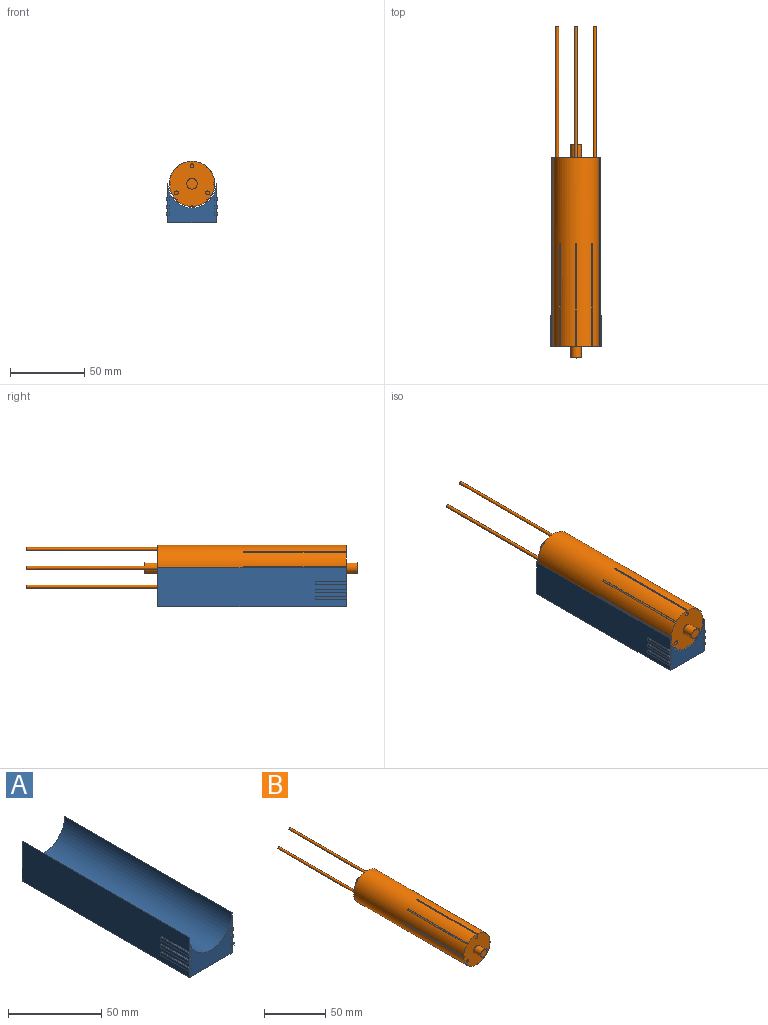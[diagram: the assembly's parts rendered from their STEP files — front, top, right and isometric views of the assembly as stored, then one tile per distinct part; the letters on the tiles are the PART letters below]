
ASSEMBLY  parts=2 mates=1
PART A: 42 faces, bbox 34.5x127.5x26.3 mm
  f0: plane 127x26.3mm, normal (-1,0,0), area 3216.9mm2, adj f1,f2,f3,f5,f6,f7,f8,f12
  f1: plane 32.51x26.3mm, normal (0,-1,0), area 428.4mm2, adj f0,f2,f3,f4,f7,f8,f9,f13
  f2: cylinder r=16.26mm len=127mm, axis (0,1,0), area 6485.9mm2, adj f0,f1,f4,f5
  f3: plane 127x32.51mm, normal (0,0,-1), area 4129mm2, adj f0,f1,f4,f5
  f4: plane 127x26.3mm, normal (1,0,0), area 3216.9mm2, adj f1,f2,f3,f5,f24,f26,f29,f30
  f5: plane 32.51x26.3mm, normal (0,1,0), area 439.8mm2, adj f0,f2,f3,f4
  f6: plane 1.96x0.98mm, normal (0,1,0), area 1.9mm2, adj f0,f7,f8,f10
  f7: plane 21.31x1.96mm, normal (0,0,1), area 21.4mm2, adj f0,f1,f6,f9,f10,f11
  f8: plane 21.31x1.96mm, normal (0,0,-1), area 21.4mm2, adj f0,f1,f6,f9,f10,f11
  f9: plane 1.96x0.48mm, normal (1,0,0), area 0.9mm2, adj f1,f7,f8,f11
  f10: plane 21.31x1.96mm, normal (-1,0,0), area 41.8mm2, adj f6,f7,f8,f11
  f11: plane 1.96x1.96mm, normal (0,-1,0), area 3.9mm2, adj f7,f8,f9,f10
  f12: plane 1.96x0.99mm, normal (0,1,0), area 1.9mm2, adj f0,f13,f14,f16
  f13: plane 21.31x1.96mm, normal (0,0,-1), area 21.6mm2, adj f0,f1,f12,f15,f16,f17
  f14: plane 21.31x1.96mm, normal (0,0,1), area 21.6mm2, adj f0,f1,f12,f15,f16,f17
  f15: plane 1.96x0.48mm, normal (1,0,0), area 0.9mm2, adj f1,f13,f14,f17
  f16: plane 21.31x1.96mm, normal (-1,0,0), area 41.8mm2, adj f12,f13,f14,f17
  f17: plane 1.96x1.96mm, normal (0,-1,0), area 3.9mm2, adj f13,f14,f15,f16
  f18: plane 1.96x1mm, normal (0,1,0), area 2mm2, adj f0,f19,f20,f22
  f19: plane 21.31x1.96mm, normal (0,0,-1), area 21.8mm2, adj f0,f1,f18,f21,f22,f23
  f20: plane 21.31x1.96mm, normal (0,0,1), area 21.8mm2, adj f0,f1,f18,f21,f22,f23
  f21: plane 1.96x0.48mm, normal (1,0,0), area 0.9mm2, adj f1,f19,f20,f23
  f22: plane 21.31x1.96mm, normal (-1,0,0), area 41.8mm2, adj f18,f19,f20,f23
  f23: plane 1.96x1.96mm, normal (0,-1,0), area 3.9mm2, adj f19,f20,f21,f22
  f24: plane 21.31x1.96mm, normal (0,0,1), area 21.6mm2, adj f1,f4,f25,f27,f28,f29
  f25: plane 1.96x0.48mm, normal (-1,0,0), area 0.9mm2, adj f1,f24,f26,f28
  f26: plane 21.31x1.96mm, normal (0,0,-1), area 21.6mm2, adj f1,f4,f25,f27,f28,f29
  f27: plane 21.31x1.96mm, normal (1,0,0), area 41.8mm2, adj f24,f26,f28,f29
  f28: plane 1.96x1.96mm, normal (0,-1,0), area 3.9mm2, adj f24,f25,f26,f27
  f29: plane 1.96x0.99mm, normal (0,1,0), area 1.9mm2, adj f4,f24,f26,f27
  f30: plane 21.31x1.96mm, normal (0,0,1), area 21.8mm2, adj f1,f4,f31,f33,f34,f35
  f31: plane 1.96x0.48mm, normal (-1,0,0), area 0.9mm2, adj f1,f30,f32,f34
  f32: plane 21.31x1.96mm, normal (0,0,-1), area 21.8mm2, adj f1,f4,f31,f33,f34,f35
  f33: plane 21.31x1.96mm, normal (1,0,0), area 41.8mm2, adj f30,f32,f34,f35
  f34: plane 1.96x1.96mm, normal (0,-1,0), area 3.9mm2, adj f30,f31,f32,f33
  f35: plane 1.96x1mm, normal (0,1,0), area 2mm2, adj f4,f30,f32,f33
  f36: plane 21.31x1.96mm, normal (0,0,1), area 21.4mm2, adj f1,f4,f37,f39,f40,f41
  f37: plane 1.96x0.48mm, normal (-1,0,0), area 0.9mm2, adj f1,f36,f38,f40
  f38: plane 21.31x1.96mm, normal (0,0,-1), area 21.4mm2, adj f1,f4,f37,f39,f40,f41
  f39: plane 21.31x1.96mm, normal (1,0,0), area 41.8mm2, adj f36,f38,f40,f41
  f40: plane 1.96x1.96mm, normal (0,-1,0), area 3.9mm2, adj f36,f37,f38,f39
  f41: plane 1.96x0.98mm, normal (0,1,0), area 1.9mm2, adj f4,f36,f38,f39
PART B: 53 faces, bbox 30.5x223.9x30.5 mm
  f0: cylinder r=15.24mm len=127mm, axis (0,1,0), area 11539.3mm2, adj f1,f2,f13,f14,f15,f17,f18,f19
  f1: plane 30.46x30.46mm, normal (0,-1,0), area 670.3mm2, adj f0,f5,f7,f9,f11,f14,f15,f16
  f2: plane 30.48x30.48mm, normal (0,1,0), area 676.7mm2, adj f0,f4,f45,f47,f49,f51
  f3: plane 7.13x7.13mm, normal (0,1,0), area 40mm2, adj f4
  f4: cylinder r=3.57mm len=9.14mm, axis (0,1,0), area 204.9mm2, adj f2,f3
  f5: cylinder r=3.57mm len=7.95mm, axis (0,1,0), area 178.2mm2, adj f1,f6
  f6: plane 7.13x7.13mm, normal (0,-1,0), area 40mm2, adj f5
  f7: cylinder r=1.27mm len=5.08mm, axis (0,-1,0), area 40.5mm2, adj f1,f8
  f8: plane 2.54x2.54mm, normal (0,-1,0), area 5.1mm2, adj f7
  f9: cylinder r=1.27mm len=5.08mm, axis (0,-1,0), area 40.5mm2, adj f1,f10
  f10: plane 2.54x2.54mm, normal (0,-1,0), area 5.1mm2, adj f9
  f11: cylinder r=1.27mm len=5.08mm, axis (0,-1,0), area 40.5mm2, adj f1,f12
  f12: plane 2.54x2.54mm, normal (0,-1,0), area 5.1mm2, adj f11
  f13: plane 1.12x1.12mm, normal (0,-1,0), area 0.5mm2, adj f0,f14,f15,f16
  f14: plane 69.09x0.32mm, normal (0.71,0,0.71), area 31.3mm2, adj f0,f1,f13,f16
  f15: plane 69.09x0.32mm, normal (-0.71,0,-0.71), area 31.3mm2, adj f0,f1,f13,f16
  f16: plane 69.09x0.8mm, normal (-0.71,0,0.71), area 77.7mm2, adj f1,f13,f14,f15
  f17: plane 1.12x0.46mm, normal (0,-1,0), area 0.5mm2, adj f0,f18,f19,f20
  f18: plane 69.09x0.45mm, normal (1,0,0), area 31.3mm2, adj f0,f1,f17,f20
  f19: plane 69.09x0.45mm, normal (-1,0,0), area 31.3mm2, adj f0,f1,f17,f20
  f20: plane 69.09x1.12mm, normal (0,0,1), area 77.7mm2, adj f1,f17,f18,f19
  f21: plane 1.12x1.12mm, normal (0,-1,0), area 0.5mm2, adj f0,f22,f23,f24
  f22: plane 69.09x0.32mm, normal (0.71,0,-0.71), area 31.3mm2, adj f0,f1,f21,f24
  f23: plane 69.09x0.32mm, normal (-0.71,0,0.71), area 31.3mm2, adj f0,f1,f21,f24
  f24: plane 69.09x0.8mm, normal (0.71,0,0.71), area 77.7mm2, adj f1,f21,f22,f23
  f25: plane 1.12x0.46mm, normal (0,-1,0), area 0.5mm2, adj f0,f26,f27,f28
  f26: plane 69.09x0.45mm, normal (0,0,-1), area 31.3mm2, adj f0,f1,f25,f28
  f27: plane 69.09x0.45mm, normal (0,0,1), area 31.3mm2, adj f0,f1,f25,f28
  f28: plane 69.09x1.12mm, normal (1,0,0), area 77.7mm2, adj f1,f25,f26,f27
  f29: plane 1.12x1.12mm, normal (0,-1,0), area 0.5mm2, adj f0,f30,f31,f32
  f30: plane 69.09x0.32mm, normal (-0.71,0,-0.71), area 31.3mm2, adj f0,f1,f29,f32
  f31: plane 69.09x0.32mm, normal (0.71,0,0.71), area 31.3mm2, adj f0,f1,f29,f32
  f32: plane 69.09x0.8mm, normal (0.71,0,-0.71), area 77.7mm2, adj f1,f29,f30,f31
  f33: plane 1.12x0.46mm, normal (0,-1,0), area 0.5mm2, adj f0,f34,f35,f36
  f34: plane 69.09x0.45mm, normal (-1,0,0), area 31.3mm2, adj f0,f1,f33,f36
  f35: plane 69.09x0.45mm, normal (1,0,0), area 31.3mm2, adj f0,f1,f33,f36
  f36: plane 69.09x1.12mm, normal (0,0,-1), area 77.7mm2, adj f1,f33,f34,f35
  f37: plane 1.12x1.12mm, normal (0,-1,0), area 0.5mm2, adj f0,f38,f39,f40
  f38: plane 69.09x0.32mm, normal (-0.71,0,0.71), area 31.3mm2, adj f0,f1,f37,f40
  f39: plane 69.09x0.32mm, normal (0.71,0,-0.71), area 31.3mm2, adj f0,f1,f37,f40
  f40: plane 69.09x0.8mm, normal (-0.71,0,-0.71), area 77.7mm2, adj f1,f37,f38,f39
  f41: plane 1.12x0.46mm, normal (0,-1,0), area 0.5mm2, adj f0,f42,f43,f44
  f42: plane 69.09x0.45mm, normal (0,0,-1), area 31.3mm2, adj f0,f1,f41,f44
  f43: plane 69.09x0.45mm, normal (0,0,1), area 31.3mm2, adj f0,f1,f41,f44
  f44: plane 69.09x1.12mm, normal (-1,0,0), area 77.7mm2, adj f1,f41,f42,f43
  f45: cylinder r=1.02mm len=88.9mm, axis (0,-1,0), area 567.5mm2, adj f2,f46
  f46: plane 2.03x2.03mm, normal (0,1,0), area 3.2mm2, adj f45
  f47: cylinder r=1.02mm len=88.9mm, axis (0,-1,0), area 567.5mm2, adj f2,f48
  f48: plane 2.03x2.03mm, normal (0,1,0), area 3.2mm2, adj f47
  f49: cylinder r=1.02mm len=88.9mm, axis (0,-1,0), area 567.5mm2, adj f2,f50
  f50: plane 2.03x2.03mm, normal (0,1,0), area 3.2mm2, adj f49
  f51: cylinder r=1.02mm len=88.9mm, axis (0,-1,0), area 567.5mm2, adj f2,f52
  f52: plane 2.03x2.03mm, normal (0,1,0), area 3.2mm2, adj f51
PLACE A t=(-30.49,34.16,-11.18)mm
PLACE B t=(-30.49,34.16,-11.18)mm
MATE fastened B.f4 <-> A.f2  axis (0,-1,0) through (-30.49,-92.84,-11.18)mm
